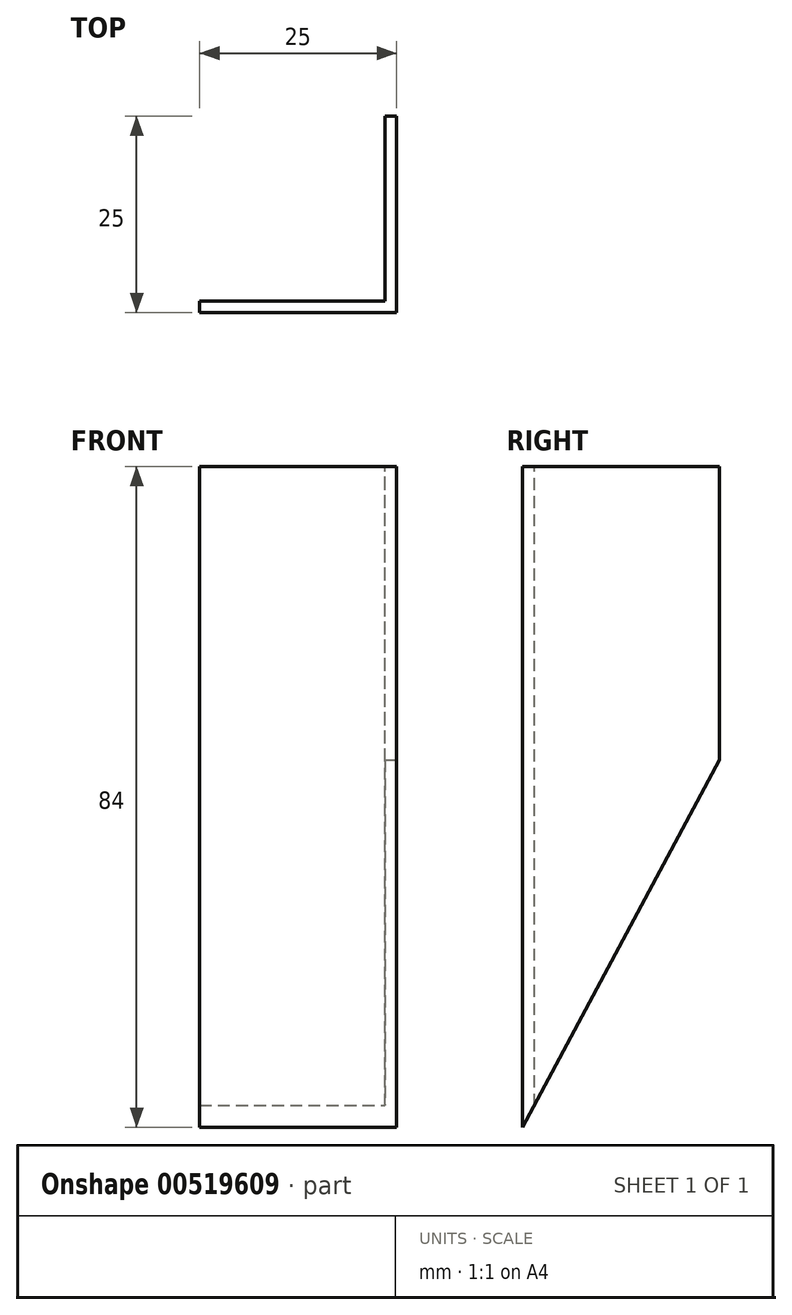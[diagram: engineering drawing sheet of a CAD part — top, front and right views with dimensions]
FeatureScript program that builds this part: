
annotation { "Feature Type Name" : "Feature", "Feature Type Description" : "" }
export const myFeature = defineFeature(function(context is Context, id is Id, definition is map)
    precondition{}
    {
        {
            var Q0;
            Q0=qCreatedBy(makeId("Top.planeOp"),FACE);
            var sketch = newSketch(context, id + "F0", { "sketchPlane" : qUnion([Q0])});
            skLineSegment(sketch, "E0.bottom", {"start": v(12.5, 0.75) * mm, "end": v(-12.5, 0.75) * mm});
            skLineSegment(sketch, "E0.top", {"start": v(12.5, -0.75) * mm, "end": v(-12.5, -0.75) * mm});
            skLineSegment(sketch, "E0.left", {"start": v(12.5, 0.75) * mm, "end": v(12.5, -0.75) * mm});
            skLineSegment(sketch, "E0.right", {"start": v(-12.5, 0.75) * mm, "end": v(-12.5, -0.75) * mm});
            skPoint(sketch, "E0.middle", {"position": v(0, 0) * mm});
            skLineSegment(sketch, "E1.bottom", {"start": v(12.5, -0.75) * mm, "end": v(11, -0.75) * mm});
            skLineSegment(sketch, "E1.top", {"start": v(12.5, 24.25) * mm, "end": v(11, 24.25) * mm});
            skLineSegment(sketch, "E1.left", {"start": v(12.5, -0.75) * mm, "end": v(12.5, 24.25) * mm});
            skLineSegment(sketch, "E1.right", {"start": v(11, -0.75) * mm, "end": v(11, 24.25) * mm});
            skSolve(sketch);
        }
        {
            var Q0;
            Q0=qSketchRegion(id+"F0",true);
            extrude(context, id + "F1", {"entities" : qUnion([Q0]), "oppositeDirection" : true, "depth" : 84 * mm, "offsetDistance" : 25 * mm});
        }
        {
            var Q0;
            Q0=makeQuery(id+"F1.opExtrude","SWEPT_FACE",FACE,{"disambiguationData":[OSD([sQuery(id+"F0.wireOp",EDGE,"E1.left")])]});
            var sketch = newSketch(context, id + "F2", { "sketchPlane" : qUnion([Q0])});
            skLineSegment(sketch, "E2", {"start": v(-0.75, -84) * mm, "end": v(-0.75, 0) * mm});
            skLineSegment(sketch, "E3", {"start": v(-0.75, 0) * mm, "end": v(44.25, 0) * mm});
            skLineSegment(sketch, "E4", {"start": v(44.25, 0) * mm, "end": v(-0.75, -84) * mm});
            skSolve(sketch);
        }
        {
            var Q0;
            {var subQ1=sQuery(id+"F0.wireOp",EDGE,"E1.left");var subQ2=makeQuery(id+"F1.opExtrude","CAP_EDGE",EDGE,{"disambiguationData":[OSD([subQ1])],"isStart":false});Q0=makeQuery(id+"F2.imprint","IMPRINT",FACE,{"disambiguationData":[TD([[makeQuery(id+"F2.imprint","IMPRINT",EDGE,{"derivedFrom":subQ2}),1.0]])]});}
            extrude(context, id + "F3", {"entities" : qUnion([Q0]), "operationType" : NewBodyOperationType.REMOVE, "oppositeDirection" : true, "depth" : 25 * mm, "offsetDistance" : 25 * mm});
        }
    });
